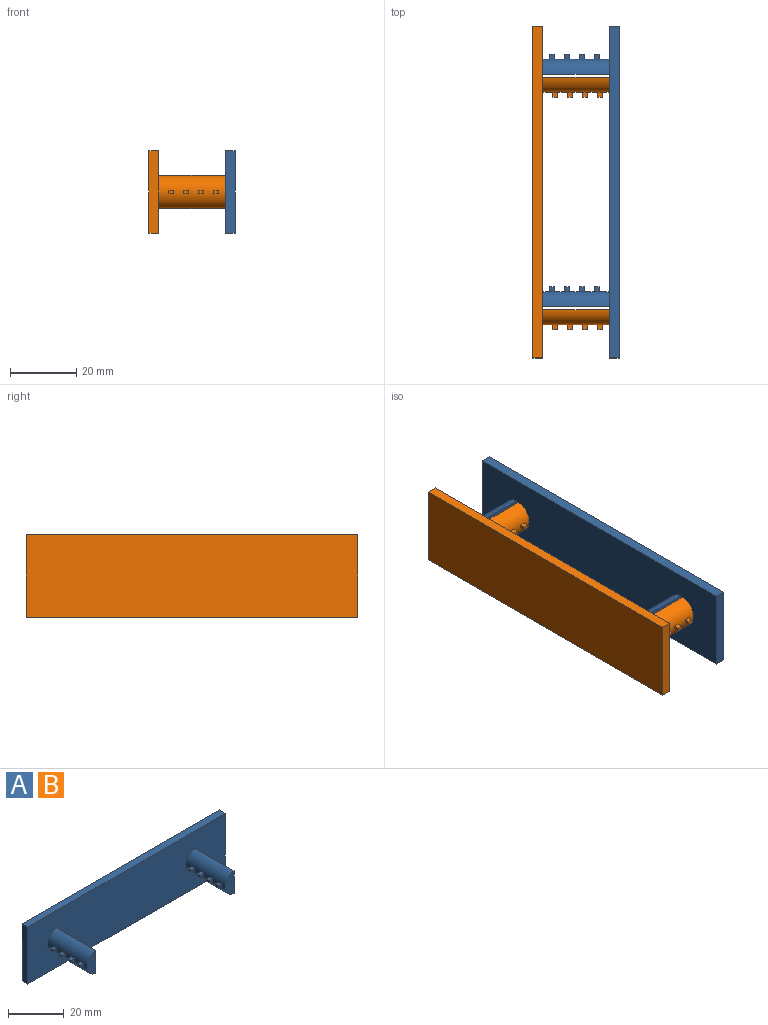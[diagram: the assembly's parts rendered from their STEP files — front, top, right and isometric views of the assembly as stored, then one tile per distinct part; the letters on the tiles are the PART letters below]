
ASSEMBLY  parts=2 mates=1
PART A: 52 faces, bbox 100x23x25 mm
  f0: cylinder r=5mm len=20mm, axis (0,1,0), area 288.1mm2, adj f2,f10,f11,f32,f33,f34,f35,f37
  f1: cylinder r=5mm len=20mm, axis (0,1,0), area 288.1mm2, adj f2,f8,f9,f12,f13,f14,f15,f17
  f2: plane 100x25mm, normal (0,-1,0), area 2431.4mm2, adj f0,f1,f3,f4,f5,f6,f8,f10
  f3: plane 100x3mm, normal (0,0,1), area 300mm2, adj f2,f4,f6,f7
  f4: plane 25x3mm, normal (-1,0,0), area 75mm2, adj f2,f3,f5,f7
  f5: plane 100x3mm, normal (0,0,-1), area 300mm2, adj f2,f4,f6,f7
  f6: plane 25x3mm, normal (1,0,0), area 75mm2, adj f2,f3,f5,f7
  f7: plane 100x25mm, normal (0,1,0), area 2500mm2, adj f3,f4,f5,f6
  f8: plane 20x9.95mm, normal (1,0,0), area 199mm2, adj f1,f2,f9
  f9: plane 9.95x4.5mm, normal (0,-1,0), area 34.3mm2, adj f1,f8
  f10: plane 20x9.95mm, normal (1,0,0), area 199mm2, adj f0,f2,f11
  f11: plane 9.95x4.5mm, normal (0,-1,0), area 34.3mm2, adj f0,f10
  f12: plane 1.53x1.5mm, normal (0,0,1), area 2.3mm2, adj f1,f14,f15,f16
  f13: plane 1.53x1.5mm, normal (0,0,-1), area 2.3mm2, adj f1,f14,f15,f16
  f14: plane 1.53x1mm, normal (0,-1,0), area 1.5mm2, adj f1,f12,f13,f16
  f15: plane 1.53x1mm, normal (0,1,0), area 1.5mm2, adj f1,f12,f13,f16
  f16: plane 1.5x1mm, normal (-1,0,0), area 1.5mm2, adj f12,f13,f14,f15
  f17: plane 1.53x1.5mm, normal (0,0,1), area 2.3mm2, adj f1,f18,f20,f21
  f18: plane 1.53x1mm, normal (0,-1,0), area 1.5mm2, adj f1,f17,f19,f21
  f19: plane 1.53x1.5mm, normal (0,0,-1), area 2.3mm2, adj f1,f18,f20,f21
  f20: plane 1.53x1mm, normal (0,1,0), area 1.5mm2, adj f1,f17,f19,f21
  f21: plane 1.5x1mm, normal (-1,0,0), area 1.5mm2, adj f17,f18,f19,f20
  f22: plane 1.53x1.5mm, normal (0,0,1), area 2.3mm2, adj f1,f23,f25,f26
  f23: plane 1.53x1mm, normal (0,-1,0), area 1.5mm2, adj f1,f22,f24,f26
  f24: plane 1.53x1.5mm, normal (0,0,-1), area 2.3mm2, adj f1,f23,f25,f26
  f25: plane 1.53x1mm, normal (0,1,0), area 1.5mm2, adj f1,f22,f24,f26
  f26: plane 1.5x1mm, normal (-1,0,0), area 1.5mm2, adj f22,f23,f24,f25
  f27: plane 1.53x1.5mm, normal (0,0,1), area 2.3mm2, adj f1,f28,f30,f31
  f28: plane 1.53x1mm, normal (0,-1,0), area 1.5mm2, adj f1,f27,f29,f31
  f29: plane 1.53x1.5mm, normal (0,0,-1), area 2.3mm2, adj f1,f28,f30,f31
  f30: plane 1.53x1mm, normal (0,1,0), area 1.5mm2, adj f1,f27,f29,f31
  f31: plane 1.5x1mm, normal (-1,0,0), area 1.5mm2, adj f27,f28,f29,f30
  f32: plane 1.53x1.5mm, normal (0,0,1), area 2.3mm2, adj f0,f34,f35,f36
  f33: plane 1.53x1.5mm, normal (0,0,-1), area 2.3mm2, adj f0,f34,f35,f36
  f34: plane 1.53x1mm, normal (0,-1,0), area 1.5mm2, adj f0,f32,f33,f36
  f35: plane 1.53x1mm, normal (0,1,0), area 1.5mm2, adj f0,f32,f33,f36
  f36: plane 1.5x1mm, normal (-1,0,0), area 1.5mm2, adj f32,f33,f34,f35
  f37: plane 1.53x1.5mm, normal (0,0,1), area 2.3mm2, adj f0,f38,f40,f41
  f38: plane 1.53x1mm, normal (0,-1,0), area 1.5mm2, adj f0,f37,f39,f41
  f39: plane 1.53x1.5mm, normal (0,0,-1), area 2.3mm2, adj f0,f38,f40,f41
  f40: plane 1.53x1mm, normal (0,1,0), area 1.5mm2, adj f0,f37,f39,f41
  f41: plane 1.5x1mm, normal (-1,0,0), area 1.5mm2, adj f37,f38,f39,f40
  f42: plane 1.53x1.5mm, normal (0,0,1), area 2.3mm2, adj f0,f43,f45,f46
  f43: plane 1.53x1mm, normal (0,-1,0), area 1.5mm2, adj f0,f42,f44,f46
  f44: plane 1.53x1.5mm, normal (0,0,-1), area 2.3mm2, adj f0,f43,f45,f46
  f45: plane 1.53x1mm, normal (0,1,0), area 1.5mm2, adj f0,f42,f44,f46
  f46: plane 1.5x1mm, normal (-1,0,0), area 1.5mm2, adj f42,f43,f44,f45
  f47: plane 1.53x1.5mm, normal (0,0,1), area 2.3mm2, adj f0,f48,f50,f51
  f48: plane 1.53x1mm, normal (0,-1,0), area 1.5mm2, adj f0,f47,f49,f51
  f49: plane 1.53x1.5mm, normal (0,0,-1), area 2.3mm2, adj f0,f48,f50,f51
  f50: plane 1.53x1mm, normal (0,1,0), area 1.5mm2, adj f0,f47,f49,f51
  f51: plane 1.5x1mm, normal (-1,0,0), area 1.5mm2, adj f47,f48,f49,f50
PART B: same geometry as A
PLACE A rot(axis=(0,0,-1),90deg) t=(23,32.61,0)mm
PLACE B rot(axis=(0,0,1),90deg) t=(-3,32.61,0)mm
MATE fastened B.f0 <-> A.f1  axis (1,0,0) through (20,-2.39,0)mm
